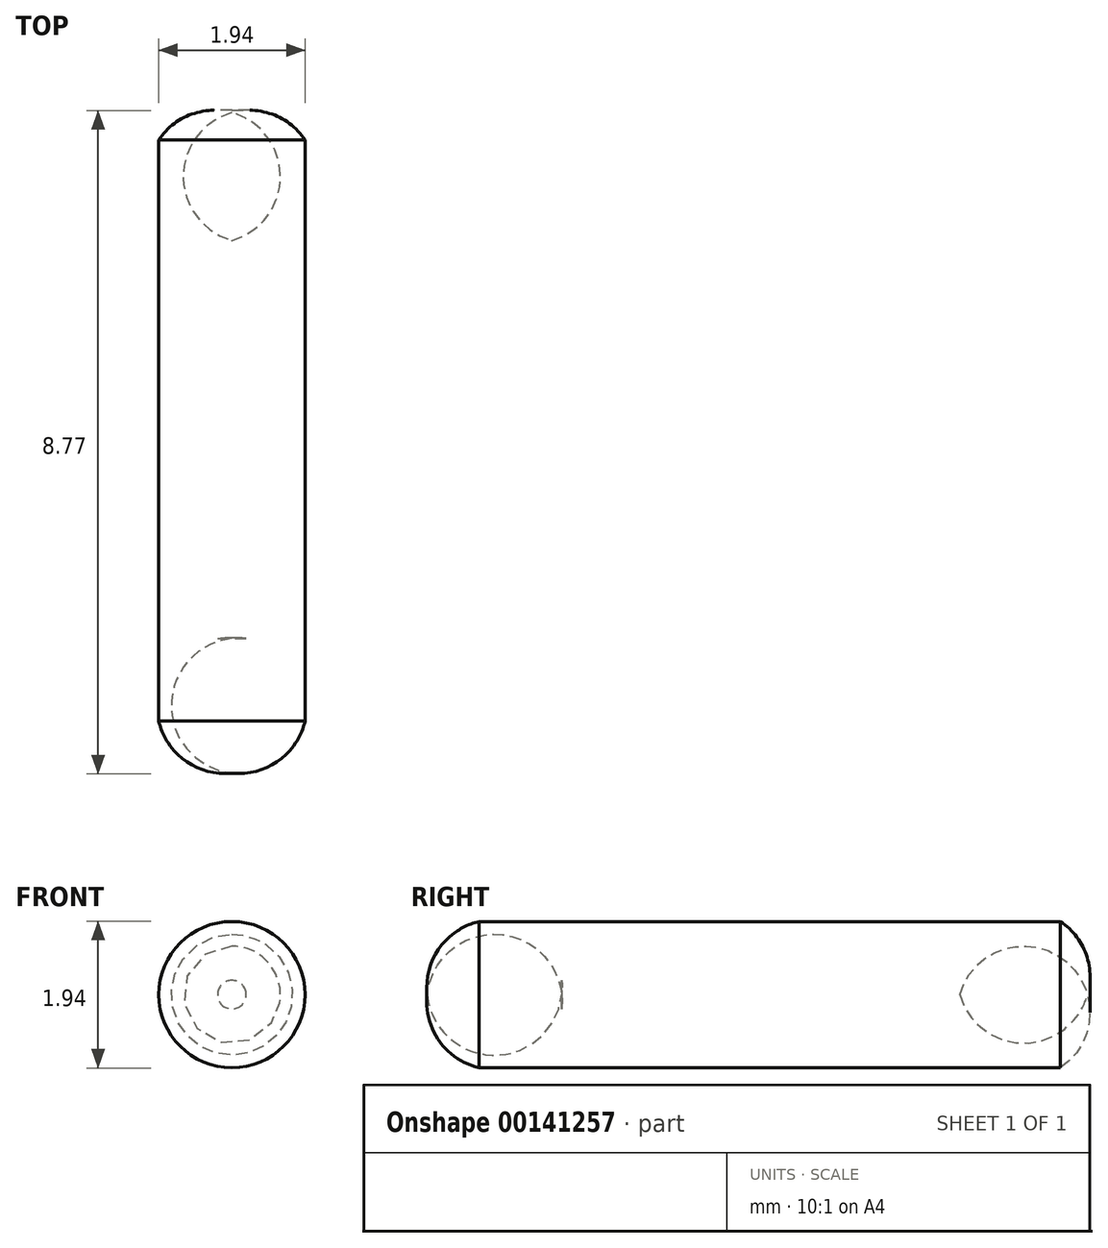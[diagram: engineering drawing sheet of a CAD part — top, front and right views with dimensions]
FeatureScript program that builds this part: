
annotation { "Feature Type Name" : "Feature", "Feature Type Description" : "" }
export const myFeature = defineFeature(function(context is Context, id is Id, definition is map)
    precondition{}
    {
        {
            var Q0;
            Q0=qCreatedBy(makeId("Top.planeOp"),FACE);
            var sketch = newSketch(context, id + "F0", { "sketchPlane" : qUnion([Q0])});
            skLineSegment(sketch, "E0", {"start": v(0, 0) * mm, "end": v(0, 8.73) * mm});
            skArc(sketch, "E1", {"start": v(0.97, 8.37) * mm, "mid": v(0.54, 8.7) * mm, "end": v(0, 8.73) * mm});
            skArc(sketch, "E2", {"start": v(0, 0) * mm, "mid": v(0.61, 0.16) * mm, "end": v(0.97, 0.69) * mm});
            skLineSegment(sketch, "E3", {"start": v(0.97, 8.37) * mm, "end": v(0.97, 0.69) * mm});
            skSolve(sketch);
        }
        {
            var Q0;
            Q0=makeQuery(id+"F0.imprint","IMPRINT",FACE,{"disambiguationData":[TD([[makeQuery(id+"F0.imprint","IMPRINT",EDGE,{"derivedFrom":sQuery(id+"F0.wireOp",EDGE,"E0")}),-1.0]])]});
            var Q1;
            Q1=sQuery(id+"F0.wireOp",EDGE,"E0");
            revolve(context, id + "F1", {"entities" : qUnion([Q0]), "axis" : qUnion([Q1]), "revolveType" : RevolveType.FULL});
        }
    });
